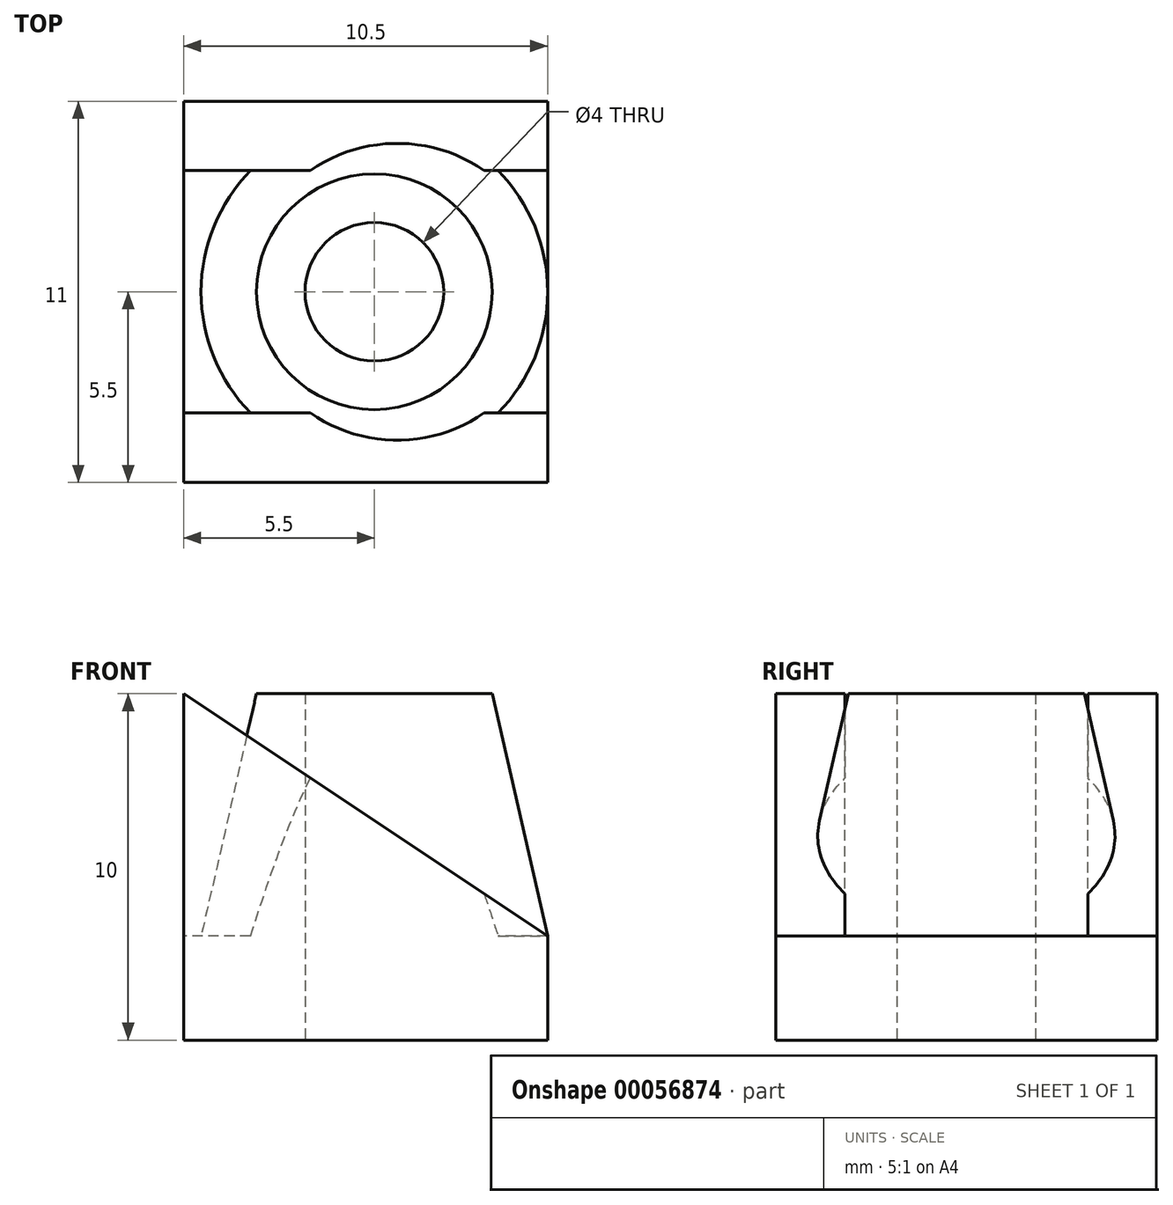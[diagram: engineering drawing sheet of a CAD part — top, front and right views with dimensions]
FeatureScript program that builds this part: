
annotation { "Feature Type Name" : "Feature", "Feature Type Description" : "" }
export const myFeature = defineFeature(function(context is Context, id is Id, definition is map)
    precondition{}
    {
        {
            var Q0;
            Q0=qCreatedBy(makeId("Front.planeOp"),FACE);
            var sketch = newSketch(context, id + "F0", { "sketchPlane" : qUnion([Q0])});
            skLineSegment(sketch, "E0", {"start": v(57.42, 0) * mm, "end": v(-61.71, 0) * mm, "construction": true});
            skLineSegment(sketch, "E1", {"start": v(0, 5) * mm, "end": v(0, -5) * mm, "construction": true});
            skLineSegment(sketch, "E2.0", {"start": v(12, 5) * mm, "end": v(-9.5, 5) * mm});
            skLineSegment(sketch, "E3.0", {"start": v(12, -5) * mm, "end": v(-9.5, -5) * mm});
            skPoint(sketch, "E4.orphan", {"position": v(0, 44.91) * mm});
            skLineSegment(sketch, "E5.0", {"start": v(-9.5, 5) * mm, "end": v(-9.5, -5) * mm, "construction": true});
            skLineSegment(sketch, "E6.0", {"start": v(12, 5) * mm, "end": v(12, -5) * mm, "construction": true});
            skLineSegment(sketch, "E7.0", {"start": v(1.5, 4) * mm, "end": v(1.5, -4) * mm, "construction": true});
            skLineSegment(sketch, "E8.0", {"start": v(-1.5, 4) * mm, "end": v(-1.5, -4) * mm, "construction": true});
            skLineSegment(sketch, "E9.0", {"start": v(57.42, 2) * mm, "end": v(-61.71, 2) * mm, "construction": true});
            skLineSegment(sketch, "E10.0", {"start": v(57.42, -2) * mm, "end": v(-61.71, -2) * mm, "construction": true});
            skLineSegment(sketch, "E11", {"start": v(12, -5) * mm, "end": v(12, -2) * mm});
            skLineSegment(sketch, "E12", {"start": v(12, -2) * mm, "end": v(1.5, -2) * mm});
            skLineSegment(sketch, "E13", {"start": v(1.5, -2) * mm, "end": v(1.5, 4) * mm});
            skLineSegment(sketch, "E14", {"start": v(-9.5, 5) * mm, "end": v(-9.5, 2) * mm});
            skLineSegment(sketch, "E15", {"start": v(-6.31, 2) * mm, "end": v(-1.5, 2) * mm});
            skLineSegment(sketch, "E16", {"start": v(-1.5, 2) * mm, "end": v(-1.5, -4) * mm});
            skLineSegment(sketch, "E17", {"start": v(-9.5, 2) * mm, "end": v(-9.5, 2) * mm});
            skLineSegment(sketch, "E18", {"start": v(1.5, 4) * mm, "end": v(1.5, 5) * mm});
            skLineSegment(sketch, "E19", {"start": v(1.5, 5) * mm, "end": v(1.5, -5) * mm});
            skLineSegment(sketch, "E20", {"start": v(-1.5, -4) * mm, "end": v(-1.5, -5) * mm});
            skLineSegment(sketch, "E21", {"start": v(1.5, 5) * mm, "end": v(12, -2) * mm});
            skArc(sketch, "E22", {"start": v(-9.5, 2) * mm, "mid": v(-7.9, 1.12) * mm, "end": v(-6.31, 2) * mm});
            skSolve(sketch);
        }
        {
            var Q0;
            {var subQ0=sQuery(id+"F0.wireOp",EDGE,"E11");Q0=makeQuery(id+"F0.imprint","IMPRINT",FACE,{"disambiguationData":[TD([[makeQuery(id+"F0.imprint","IMPRINT",EDGE,{"derivedFrom":subQ0}),1.0]])]});}
            var Q1;
            {var subQ0=sQuery(id+"F0.wireOp",EDGE,"E14");Q1=makeQuery(id+"F0.imprint","IMPRINT",FACE,{"disambiguationData":[TD([[makeQuery(id+"F0.imprint","IMPRINT",EDGE,{"derivedFrom":subQ0}),1.0]])]});}
            extrude(context, id + "F1", {"entities" : qUnion([Q0, Q1]), "depth" : 11 * mm});
        }
        {
            var Q0;
            Q0=makeQuery(id+"F0.imprint","IMPRINT",FACE,{"disambiguationData":[TD([[makeQuery(id+"F0.imprint","IMPRINT",EDGE,{"derivedFrom":sQuery(id+"F0.wireOp",EDGE,"E12")}),-1.0]])]});
            extrude(context, id + "F2", {"entities" : qUnion([Q0]), "operationType" : NewBodyOperationType.ADD, "depth" : 2 * mm});
        }
        {
            var Q0;
            Q0=makeQuery(id+"F1.opExtrude","CAP_FACE",FACE,{"disambiguationData":[OSD([sQuery(id+"F0.wireOp",EDGE,"E2.0"),sQuery(id+"F0.wireOp",EDGE,"E3.0"),sQuery(id+"F0.wireOp",EDGE,"E11"),sQuery(id+"F0.wireOp",EDGE,"E12"),sQuery(id+"F0.wireOp",EDGE,"E14"),sQuery(id+"F0.wireOp",EDGE,"E15"),sQuery(id+"F0.wireOp",EDGE,"E16"),sQuery(id+"F0.wireOp",EDGE,"E19"),sQuery(id+"F0.wireOp",EDGE,"E20"),sQuery(id+"F0.wireOp",EDGE,"E22")])],"isStart":false});
            var sketch = newSketch(context, id + "F3", { "sketchPlane" : qUnion([Q0])});
            skLineSegment(sketch, "E23.0.0", {"start": v(-1.5, -5) * mm, "end": v(12, -5) * mm});
            skLineSegment(sketch, "E23.0.1", {"start": v(12, -5) * mm, "end": v(12, -2) * mm});
            skLineSegment(sketch, "E23.0.2", {"start": v(12, -2) * mm, "end": v(1.5, -2) * mm});
            skLineSegment(sketch, "E23.0.3", {"start": v(1.5, -2) * mm, "end": v(1.5, 5) * mm});
            skLineSegment(sketch, "E23.0.4", {"start": v(1.5, 5) * mm, "end": v(-9.5, 5) * mm});
            skLineSegment(sketch, "E23.0.5", {"start": v(-9.5, 5) * mm, "end": v(-9.5, 2) * mm});
            skArc(sketch, "E23.0.6", {"start": v(-9.5, 2) * mm, "mid": v(-7.9, 1.12) * mm, "end": v(-6.31, 2) * mm});
            skLineSegment(sketch, "E23.0.7", {"start": v(-6.31, 2) * mm, "end": v(-1.5, 2) * mm});
            skLineSegment(sketch, "E23.0.8", {"start": v(-1.5, 2) * mm, "end": v(-1.5, -5) * mm});
            skLineSegment(sketch, "E24", {"start": v(1.5, 5) * mm, "end": v(12, -2) * mm});
            skLineSegment(sketch, "E25", {"start": v(1.5, -2) * mm, "end": v(12, -2) * mm});
            skSolve(sketch);
        }
        {
            var Q0;
            Q0=makeQuery(id+"F3.imprint","IMPRINT",FACE,{"disambiguationData":[TD([[makeQuery(id+"F3.imprint","IMPRINT",EDGE,{"derivedFrom":sQuery(id+"F3.wireOp",EDGE,"E24")}),-1.0]])]});
            extrude(context, id + "F4", {"entities" : qUnion([Q0]), "operationType" : NewBodyOperationType.ADD, "oppositeDirection" : true, "depth" : 2 * mm});
        }
        {
            var Q0;
            Q0=makeQuery(id+"F1.opExtrude","SWEPT_FACE",FACE,{"disambiguationData":[OSD([sQuery(id+"F0.wireOp",EDGE,"E3.0")])]});
            var sketch = newSketch(context, id + "F5", { "sketchPlane" : qUnion([Q0])});
            skLineSegment(sketch, "E26.0.0", {"start": v(-1.5, 0) * mm, "end": v(12, 0) * mm});
            skLineSegment(sketch, "E26.0.1", {"start": v(12, 0) * mm, "end": v(12, 11) * mm});
            skLineSegment(sketch, "E26.0.2", {"start": v(12, 11) * mm, "end": v(-1.5, 11) * mm});
            skLineSegment(sketch, "E26.0.3", {"start": v(-1.5, 11) * mm, "end": v(-1.5, 0) * mm});
            skLineSegment(sketch, "E27", {"start": v(12, 5.5) * mm, "end": v(-1.5, 5.5) * mm, "construction": true});
            skLineSegment(sketch, "E28.0", {"start": v(7, 0) * mm, "end": v(7, 11) * mm, "construction": true});
            skCircle(sketch, "E29", {"center": v(7, 5.5) * mm, "radius": 2 * mm});
            skPoint(sketch, "E30.0", {"position": v(0, 0) * mm});
            skSolve(sketch);
        }
        {
            var Q0;
            Q0=makeQuery(id+"F5.imprint","IMPRINT",FACE,{"disambiguationData":[TD([[makeQuery(id+"F5.imprint","IMPRINT",EDGE,{"derivedFrom":sQuery(id+"F5.wireOp",EDGE,"E29")}),1.0]])]});
            extrude(context, id + "F6", {"entities" : qUnion([Q0]), "operationType" : NewBodyOperationType.REMOVE, "oppositeDirection" : true, "depth" : 25 * mm});
        }
        {
            var Q0;
            Q0=makeQuery(id+"F1.opExtrude","SWEPT_FACE",FACE,{"disambiguationData":[OSD([sQuery(id+"F0.wireOp",EDGE,"E12")])]});
            var sketch = newSketch(context, id + "F7", { "sketchPlane" : qUnion([Q0])});
            skCircle(sketch, "E31.0", {"center": v(7, -5.5) * mm, "radius": 2 * mm});
            skCircle(sketch, "E32", {"center": v(7, -5.5) * mm, "radius": 5 * mm});
            skCircle(sketch, "E33", {"center": v(7, -5.5) * mm, "radius": 3.4 * mm});
            skSolve(sketch);
        }
        {
            var Q0;
            Q0=makeQuery(id+"F7.imprint","IMPRINT",FACE,{"disambiguationData":[TD([[makeQuery(id+"F7.imprint","IMPRINT",EDGE,{"derivedFrom":sQuery(id+"F7.wireOp",EDGE,"E31.0")}),1.0]])]});
            extrude(context, id + "F8", {"entities" : qUnion([Q0]), "operationType" : NewBodyOperationType.ADD, "depth" : 7 * mm});
        }
        {
            var Q0;
            Q0=qCreatedBy(makeId("Right.planeOp"),FACE);
            cPlane(context, id + "F9", {"entities" : qUnion([Q0]), "cplaneType" : CPlaneType.OFFSET, "offset" : 7 * mm, "width" : 150 * mm, "height" : 150 * mm});
        }
        {
            var Q0;
            Q0=qCreatedBy(id+"F9.planeOp",FACE);
            var sketch = newSketch(context, id + "F10", { "sketchPlane" : qUnion([Q0])});
            skLineSegment(sketch, "E34.0", {"start": v(-3.5, -5) * mm, "end": v(-7.5, -5) * mm});
            skLineSegment(sketch, "E35.0", {"start": v(-8.9, -2) * mm, "end": v(-2.1, -2) * mm});
            skLineSegment(sketch, "E36.0", {"start": v(-9, -2) * mm, "end": v(-2, -2) * mm});
            skLineSegment(sketch, "E37.0", {"start": v(-10.5, -2) * mm, "end": v(-0.5, -2) * mm});
            skPoint(sketch, "E38.0", {"position": v(-5.5, -2) * mm});
            skLineSegment(sketch, "E39", {"start": v(-5.5, -2) * mm, "end": v(9, -2) * mm});
            skLineSegment(sketch, "E40.0.0", {"start": v(-8.9, 5) * mm, "end": v(-2.1, 5) * mm});
            skLineSegment(sketch, "E41", {"start": v(-2.1, 5) * mm, "end": v(-0.5, -2) * mm});
            skLineSegment(sketch, "E42", {"start": v(-2.1, -2) * mm, "end": v(-2.1, 5) * mm});
            skLineSegment(sketch, "E43", {"start": v(-2.1, -2) * mm, "end": v(-0.5, -2) * mm});
            skLineSegment(sketch, "E44", {"start": v(-5.5, -2) * mm, "end": v(-5.5, 5.43) * mm});
            skPoint(sketch, "E44.endSnap0", {"position": v(-5.5, 5) * mm});
            skSolve(sketch);
        }
        {
            var Q0;
            {var subQ0=sQuery(id+"F10.wireOp",EDGE,"E41");Q0=makeQuery(id+"F10.imprint","IMPRINT",FACE,{"disambiguationData":[TD([[makeQuery(id+"F10.imprint","IMPRINT",EDGE,{"derivedFrom":subQ0}),-1.0]])]});}
            var Q1;
            Q1=sQuery(id+"F10.wireOp",EDGE,"E44");
            revolve(context, id + "F11", {"operationType" : NewBodyOperationType.ADD, "entities" : qUnion([Q0]), "axis" : qUnion([Q1]), "revolveType" : RevolveType.FULL});
        }
    });
